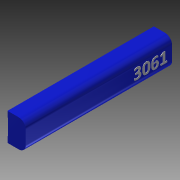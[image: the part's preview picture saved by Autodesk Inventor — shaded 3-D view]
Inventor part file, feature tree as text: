
AUTODESK INVENTOR PART (.ipt)
format: ipt  version: 2014 SP1 (Build 180222100, 222)  size: 300,544 bytes
history: native  units: in
note: dims shown in document units (in); Inventor stores cm internally (conversion verified against a paired STEP export)
features: extrude x4, reference x4, sketch x3, projected_geometry x1
ambient origin geometry x8: Origin, YZ Plane, XZ Plane, XY Plane, X Axis, Y Axis, Z Axis, Center Point
bodies: Solid1 (feature_tree)
feature tree (12):
  sketch  "Sketch1"  dims[d0=0.0625in d1=0.0in d3=1.0in]
  extrude  "Extrusion1"  Depth=1.0in
  extrude  "Extrusion2"  Depth=0.0625in
  extrude  "Extrusion3"  Depth=0.0625in TaperAngle=0.0deg
  extrude  "Extrusion5"  Depth=6.0in
  reference  "Reference4"
  reference  "Reference5"
  sketch  "Sketch2"  dims[d7=1.0in d9=0.0625in]
  sketch  "Sketch3"  dims[d10=26.875in d11=0.0in d12=0.0625in d13=0.0in d42=6.0in d43=0.0625in d44=0.0in d45=0.0625in d46=0.0625in d47=1.0in d48=2.5in]
  reference  "Reference6"
  projected_geometry  "Projected Loop1"
  reference  "Reference7"
